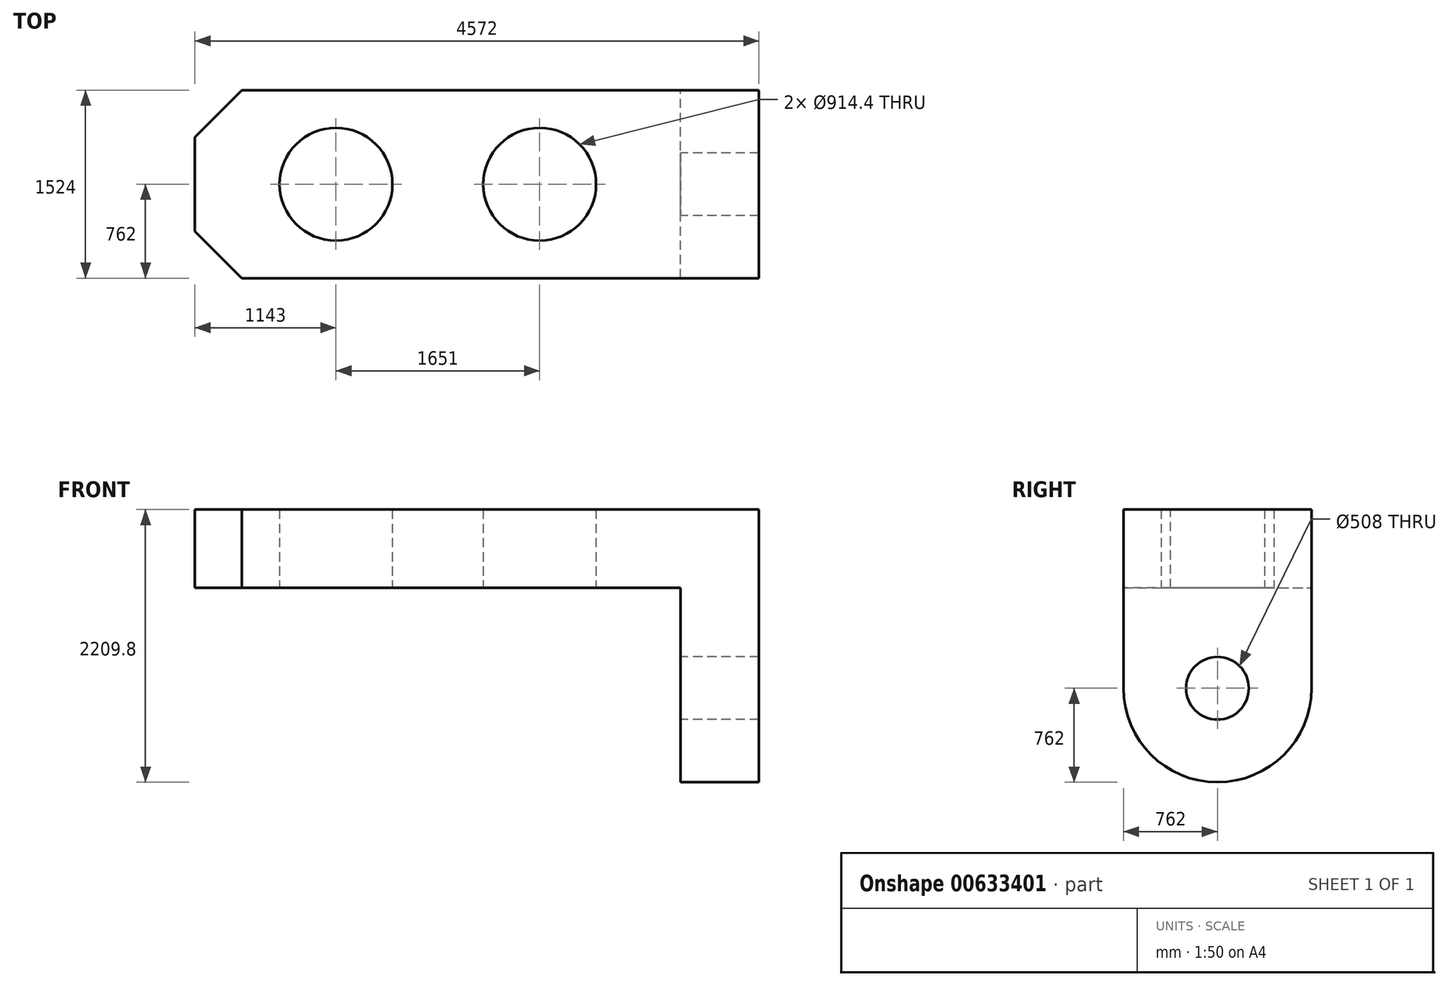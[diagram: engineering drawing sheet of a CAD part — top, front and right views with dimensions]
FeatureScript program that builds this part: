
annotation { "Feature Type Name" : "Feature", "Feature Type Description" : "" }
export const myFeature = defineFeature(function(context is Context, id is Id, definition is map)
    precondition{}
    {
        {
            var Q0;
            Q0=qCreatedBy(makeId("Top.planeOp"),FACE);
            var sketch = newSketch(context, id + "F0", { "sketchPlane" : qUnion([Q0])});
            skLineSegment(sketch, "E0.bottom", {"start": v(-4572, 1524) * mm, "end": v(0, 1524) * mm});
            skLineSegment(sketch, "E0.top", {"start": v(-4572, 0) * mm, "end": v(0, 0) * mm});
            skLineSegment(sketch, "E0.left", {"start": v(-4572, 1524) * mm, "end": v(-4572, 0) * mm});
            skLineSegment(sketch, "E0.right", {"start": v(0, 1524) * mm, "end": v(0, 0) * mm});
            skSolve(sketch);
        }
        {
            var Q0;
            Q0 = qSketchRegion(id + "F0", true);
            extrude(context, id + "F1", {"entities" : qUnion([Q0]), "depth" : 635 * mm, "offsetDistance" : 25.4 * mm});
        }
        {
            var Q0;
            Q0=makeQuery(id+"F1.opExtrude","CAP_FACE",FACE,{"disambiguationData":[OSD([sQuery(id+"F0.wireOp",EDGE,"E0.bottom"),sQuery(id+"F0.wireOp",EDGE,"E0.top"),sQuery(id+"F0.wireOp",EDGE,"E0.left"),sQuery(id+"F0.wireOp",EDGE,"E0.right")])],"isStart":true});
            var sketch = newSketch(context, id + "F2", { "sketchPlane" : qUnion([Q0])});
            skLineSegment(sketch, "E1.bottom", {"start": v(0, 0) * mm, "end": v(-635, 0) * mm});
            skLineSegment(sketch, "E1.top", {"start": v(0, -1524) * mm, "end": v(-635, -1524) * mm});
            skLineSegment(sketch, "E1.left", {"start": v(0, 0) * mm, "end": v(0, -1524) * mm});
            skLineSegment(sketch, "E1.right", {"start": v(-635, 0) * mm, "end": v(-635, -1524) * mm});
            skSolve(sketch);
        }
        {
            var Q0;
            Q0 = qSketchRegion(id + "F2", true);
            extrude(context, id + "F3", {"entities" : qUnion([Q0]), "operationType" : NewBodyOperationType.ADD, "depth" : 1574.8 * mm, "offsetDistance" : 25.4 * mm});
        }
        {
            var Q0;
            Q0=makeQuery(id+"F3.opExtrude","CAP_EDGE",EDGE,{"disambiguationData":[OSD([sQuery(id+"F2.wireOp",EDGE,"E1.bottom")])],"isStart":false});
            var Q1;
            Q1=makeQuery(id+"F3.opExtrude","CAP_EDGE",EDGE,{"disambiguationData":[OSD([sQuery(id+"F2.wireOp",EDGE,"E1.top")])],"isStart":false});
            fillet(context, id + "F4", {"entities" : qUnion([Q0, Q1]), "radius" : 762 * mm, "tangentPropagation" : true, "allowEdgeOverflow" : false});
        }
        {
            var Q0;
            Q0=makeQuery(id+"F1.opExtrude","CAP_FACE",FACE,{"disambiguationData":[OSD([sQuery(id+"F0.wireOp",EDGE,"E0.bottom"),sQuery(id+"F0.wireOp",EDGE,"E0.top"),sQuery(id+"F0.wireOp",EDGE,"E0.left"),sQuery(id+"F0.wireOp",EDGE,"E0.right")])],"isStart":true});
            var sketch = newSketch(context, id + "F5", { "sketchPlane" : qUnion([Q0])});
            skCircle(sketch, "E2", {"center": v(-1778, -762) * mm, "radius": 457.2 * mm});
            skPoint(sketch, "E2.centerSnap0", {"position": v(-635, -762) * mm});
            skCircle(sketch, "E3", {"center": v(-3429, -762) * mm, "radius": 457.2 * mm});
            skSolve(sketch);
        }
        {
            var Q0;
            Q0=makeQuery(id+"F5.imprint","IMPRINT",FACE,{"disambiguationData":[TD([[makeQuery(id+"F5.imprint","IMPRINT",EDGE,{"derivedFrom":sQuery(id+"F5.wireOp",EDGE,"E2")}),1.0]])]});
            var Q1;
            Q1=makeQuery(id+"F5.imprint","IMPRINT",FACE,{"disambiguationData":[TD([[makeQuery(id+"F5.imprint","IMPRINT",EDGE,{"derivedFrom":sQuery(id+"F5.wireOp",EDGE,"E3")}),1.0]])]});
            extrude(context, id + "F6", {"entities" : qUnion([Q0, Q1]), "operationType" : NewBodyOperationType.REMOVE, "oppositeDirection" : true, "depth" : 635 * mm, "offsetDistance" : 25.4 * mm});
        }
        {
            var Q0;
            Q0=makeQuery(id+"F3.opExtrude","SWEPT_FACE",FACE,{"disambiguationData":[OSD([sQuery(id+"F2.wireOp",EDGE,"E1.right")])]});
            var sketch = newSketch(context, id + "F7", { "sketchPlane" : qUnion([Q0])});
            skCircle(sketch, "E4", {"center": v(-762, -812.8) * mm, "radius": 254 * mm});
            skSolve(sketch);
        }
        {
            var Q0;
            Q0=makeQuery(id+"F7.imprint","IMPRINT",FACE,{"disambiguationData":[TD([[makeQuery(id+"F7.imprint","IMPRINT",EDGE,{"derivedFrom":sQuery(id+"F7.wireOp",EDGE,"E4")}),1.0]])]});
            extrude(context, id + "F8", {"entities" : qUnion([Q0]), "operationType" : NewBodyOperationType.REMOVE, "endBound" : BoundingType.UP_TO_NEXT, "oppositeDirection" : true, "depth" : 25.4 * mm, "offsetDistance" : 25.4 * mm});
        }
        {
            var Q0;
            Q0=makeQuery(id+"F1.opExtrude","SWEPT_EDGE",EDGE,{"disambiguationData":[OSD([sQuery(id+"F0.wireOp",EDGE,"E0.top"),sQuery(id+"F0.wireOp",EDGE,"E0.left")])]});
            var Q1;
            Q1=makeQuery(id+"F1.opExtrude","SWEPT_EDGE",EDGE,{"disambiguationData":[OSD([sQuery(id+"F0.wireOp",EDGE,"E0.bottom"),sQuery(id+"F0.wireOp",EDGE,"E0.left")])]});
            chamfer(context, id + "F9", {"entities" : qUnion([Q0, Q1]), "width" : 381 * mm, "tangentPropagation" : true});
        }
    });
